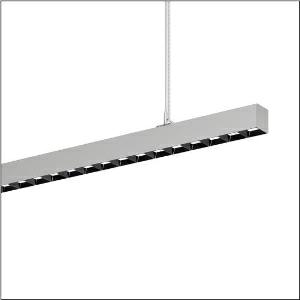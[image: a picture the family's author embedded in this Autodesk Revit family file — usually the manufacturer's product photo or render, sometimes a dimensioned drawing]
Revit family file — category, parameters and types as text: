
# Revit family: silica_r__21_51mx32dc4dsb_d767
name_source: partatom
category: Lighting Fixtures
units: mm (PartAtom-declared; Revit-internal decimal feet)

## family parameters
Cut with Voids When Loaded = No
Host = Face
Light Source = No
Part Type = Normal
Room Calculation Point = No
Round Connector Dimension = Use Diameter
Shared = No

## types (1)
- --- (1 x LED, 18230 lm, 105.8 W, 4000K)
    Apparent Load = 106 VA
    CIE Flux Codes = 86 99 100 59 100
    Color Rendering = 80
    Color Temperature = 4000K
    Default Elevation = 1800 mm
    Description = Silica® 21, office luminaire, primary light control with darklight reflector, of PMMA, black, CAT 2 (L<= 3000cd/m²), light emission: direct/indirect distribution, primary light characteristic: symmetric, installation type: suspended mounting, LED, rated luminous flux: 18.230lm, luminous efficacy: 172lm/W, light colour: 840, colour temperature: 4000K, with terminal, 3+2-pole, max. 2.5mm², mains connection: 220..240V, AC, 50/60Hz, rated input power: 105.8W, luminaire housing, of aluminium, metallic grey (RAL 9006), length: 3.004mm, width: 53mm, height: 53mm, protection rating (complete): IP20, insulation class (complete): insulation class I (protective earthing), certification: CE, permissible operating ambient temperature: 0..+35°C, standard: EN 50419, packaging unit: 1 piece
    Height = 53 mm
    Lamp = 1 x LED
    Lamp Light Flux = 18230 lm
    Lamp Power = 105.8 W
    Lamp count = 1
    Length = 3004 mm
    Luminous efficacy = 172 lm/W
    Manufacturer = Siteco
    ModVariant = No
    Model = 51MX32DC4DSB
    Mounting Place = Ceiling
    Mounting Type = Pendant
    Number of Poles = 1
    OnlyDefault = Yes
    Power Factor = 1
    Product Name = Silica® 21
    Product group = office luminaire | ceiling pendant
    ProductGroupID = 902
    Protection Class = Protection class I
    Protection Degree = IP 20
    RLX_Detail_Level = 1
    RLX_Emergency_Light_Flux = 0 lm
    RLX_Emergency_Type = 0
    RLX_Emergency_Type_DB = No
    RlxData = <blob elided: 66349 chars, md5=bb68e322>
    Socket = socket
    Standby Power = 0 W
    System Light Flux = 18230 lm
    System Power = 106 W
    Type Comments = factory setting: luminous flux: 100 % | dim-lin: 254 | 366 mA
    Type Image = l_1335859.jpg
    URL = http://relux.com
    VarID = @adj_091487
    Voltage = 0 V
    Weight = 0.00 kg
    Width = 53 mm

## geometry (parser evidence)
native form markers: Blend x4, Sweep x10
no freeform markers — native parametric forms only
